# Revit family: Lighting-Troffer-Cooper-Corelite-Class-R2X-1X4-LED
name_source: partatom
category: Lighting Fixtures
revit_build: Autodesk Revit 2014 (Build: 20130308_1515(x64)
units: mm (PartAtom-declared; Revit-internal decimal feet)

## types (45) — shared parameters
Assembly Code = D5020200
Color Filter = 16777215
Connector Description = Power In
Default Elevation = 0' - 0"
Description = Shallow Recessed - LED
Dimming Lamp Color Temperature Shift = <None>
Emit Shape Visible in Rendering = Yes
Emit from Rectangle Length = 0' - 1"
Emit from Rectangle Width = 3' - 10 7/8"
Fixture Height = 0' - 2 7/8"
Fixture Length = 3' - 11 3/4"
Fixture Width = 0' - 11 3/4"
Installation Type = Recessed
Lamp = LED
Manufacturer = Cooper Lighting
Model = Class R2X
Photometric Web File = Select File
Product Page URL = http://www.cooperindustries.com
Tilt Angle = 90.00°
Type Comments = 1' X 4'
URL = http://www.cooperindustries.com

## per-type parameters (varying)
| type | Apparent Load | Voltage |
| 1' X 4'_WO_120V_3000K_Light Level 1 | 33 VA | 120 V |
| 1' X 4'_WO_277V_3000K_Light Level 1 | 33 VA | 277 V |
| 1' X 4'_WO_347V_3000K_Light Level 1 | 33 VA | 347 V |
| 1' X 4'_WO_120V_3000K_Light Level 2 | 48 VA | 120 V |
| 1' X 4'_WO_277V_3000K_Light Level 2 | 48 VA | 277 V |
| 1' X 4'_WO_347V_3000K_Light Level 2 | 48 VA | 347 V |
| 1' X 4'_WO_120V_3000K_Light Level 3 | 58 VA | 120 V |
| 1' X 4'_WO_277V_3000K_Light Level 3 | 58 VA | 277 V |
| 1' X 4'_WO_347V_3000K_Light Level 3 | 58 VA | 347 V |
| 1' X 4'_WO_120V_3000K_Light Level 4 | 76 VA | 120 V |
| 1' X 4'_WO_277V_3000K_Light Level 4 | 76 VA | 277 V |
| 1' X 4'_WO_347V_3000K_Light Level 4 | 76 VA | 347 V |
| 1' X 4'_WO_120V_3000K_Light Level 5 | 97 VA | 120 V |
| 1' X 4'_WO_277V_3000K_Light Level 5 | 97 VA | 277 V |
| 1' X 4'_WO_347V_3000K_Light Level 5 | 97 VA | 347 V |
| 1' X 4'_WO_120V_3500K_Light Level 1 | 33 VA | 120 V |
| 1' X 4'_WO_277V_3500K_Light Level 1 | 33 VA | 277 V |
| 1' X 4'_WO_347V_3500K_Light Level 1 | 33 VA | 347 V |
| 1' X 4'_WO_120V_3500K_Light Level 2 | 48 VA | 120 V |
| 1' X 4'_WO_277V_3500K_Light Level 2 | 48 VA | 277 V |
| 1' X 4'_WO_347V_3500K_Light Level 2 | 48 VA | 347 V |
| 1' X 4'_WO_120V_3500K_Light Level 3 | 58 VA | 120 V |
| 1' X 4'_WO_277V_3500K_Light Level 3 | 58 VA | 277 V |
| 1' X 4'_WO_347V_3500K_Light Level 3 | 58 VA | 347 V |
| 1' X 4'_WO_120V_3500K_Light Level 4 | 76 VA | 120 V |
| 1' X 4'_WO_277V_3500K_Light Level 4 | 76 VA | 277 V |
| 1' X 4'_WO_347V_3500K_Light Level 4 | 76 VA | 347 V |
| 1' X 4'_WO_120V_3500K_Light Level 5 | 97 VA | 120 V |
| 1' X 4'_WO_277V_3500K_Light Level 5 | 97 VA | 277 V |
| 1' X 4'_WO_347V_3500K_Light Level 5 | 97 VA | 347 V |
| 1' X 4'_WO_120V_4000K_Light Level 1 | 33 VA | 120 V |
| 1' X 4'_WO_277V_4000K_Light Level 1 | 33 VA | 277 V |
| 1' X 4'_WO_347V_4000K_Light Level 1 | 33 VA | 347 V |
| 1' X 4'_WO_120V_4000K_Light Level 2 | 48 VA | 120 V |
| 1' X 4'_WO_277V_4000K_Light Level 2 | 48 VA | 277 V |
| 1' X 4'_WO_347V_4000K_Light Level 2 | 48 VA | 347 V |
| 1' X 4'_WO_120V_4000K_Light Level 3 | 58 VA | 120 V |
| 1' X 4'_WO_277V_4000K_Light Level 3 | 58 VA | 277 V |
| 1' X 4'_WO_347V_4000K_Light Level 3 | 58 VA | 347 V |
| 1' X 4'_WO_120V_4000K_Light Level 4 | 76 VA | 120 V |
| 1' X 4'_WO_277V_4000K_Light Level 4 | 76 VA | 277 V |
| 1' X 4'_WO_347V_4000K_Light Level 4 | 76 VA | 347 V |
| 1' X 4'_WO_120V_4000K_Light Level 5 | 97 VA | 120 V |
| 1' X 4'_WO_277V_4000K_Light Level 5 | 97 VA | 277 V |
| 1' X 4'_WO_347V_4000K_Light Level 5 | 97 VA | 347 V |

## geometry (parser evidence)
native form markers: Blend x1, Sweep x1
no freeform markers — native parametric forms only
